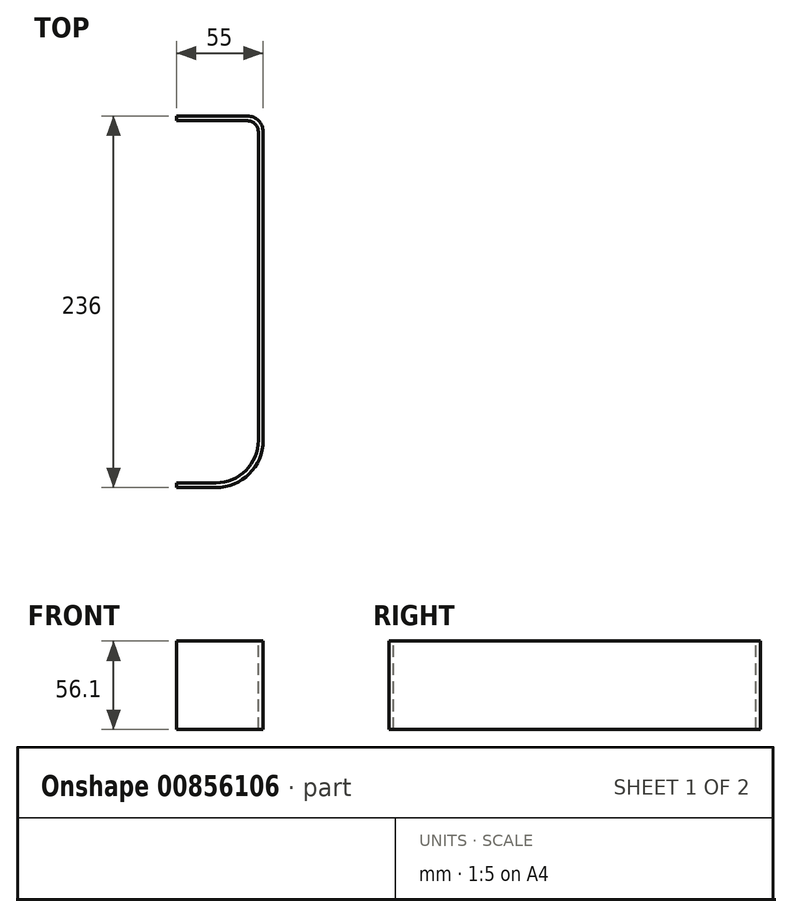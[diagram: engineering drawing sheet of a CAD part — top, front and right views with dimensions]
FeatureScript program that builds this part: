
annotation { "Feature Type Name" : "Feature", "Feature Type Description" : "" }
export const myFeature = defineFeature(function(context is Context, id is Id, definition is map)
    precondition{}
    {
        {
            var Q0;
            Q0=qCreatedBy(makeId("Top.planeOp"),FACE);
            var sketch = newSketch(context, id + "F0", { "sketchPlane" : qUnion([Q0])});
            skLineSegment(sketch, "E0.1", {"start": v(0, 0) * mm, "end": v(0, 0) * mm});
            skPoint(sketch, "E1", {"position": v(265.17, 265.17) * mm});
            skPoint(sketch, "E2", {"position": v(-265.17, 265.17) * mm});
            skPoint(sketch, "E3", {"position": v(265.17, -265.17) * mm});
            skCircle(sketch, "E4", {"center": v(265.17, 265.17) * mm, "radius": 234.95 * mm, "construction": true});
            skCircle(sketch, "E5", {"center": v(265.17, -265.17) * mm, "radius": 234.95 * mm, "construction": true});
            skCircle(sketch, "E6", {"center": v(265.17, 265.17) * mm, "radius": 30.35 * mm, "construction": true});
            skCircle(sketch, "E7", {"center": v(265.17, -265.17) * mm, "radius": 30.35 * mm, "construction": true});
            skLineSegment(sketch, "E8", {"start": v(0, 0) * mm, "end": v(265.17, 265.17) * mm, "construction": true});
            skLineSegment(sketch, "E9", {"start": v(0, 0) * mm, "end": v(265.17, -265.17) * mm, "construction": true});
            skArc(sketch, "E10", {"start": v(-265.17, 265.17) * mm, "mid": v(265.17, 265.17) * mm, "end": v(265.17, -265.17) * mm, "construction": true});
            skPoint(sketch, "E11", {"position": v(235.63, -235.63) * mm});
            skLineSegment(sketch, "E12", {"start": v(242.7, -228.56) * mm, "end": v(217.95, -203.81) * mm});
            skLineSegment(sketch, "E13", {"start": v(217.95, -203.81) * mm, "end": v(203.81, -217.95) * mm});
            skLineSegment(sketch, "E14", {"start": v(242.7, -228.56) * mm, "end": v(228.56, -242.7) * mm});
            skLineSegment(sketch, "E15", {"start": v(228.56, -242.7) * mm, "end": v(203.81, -217.95) * mm});
            skLineSegment(sketch, "E16.left", {"start": v(55, -103) * mm, "end": v(55, 93) * mm});
            skPoint(sketch, "E17.visualSharp", {"position": v(55, -133) * mm});
            skArc(sketch, "E17.filletArc", {"start": v(25, -133) * mm, "mid": v(46.21, -124.21) * mm, "end": v(55, -103) * mm});
            skPoint(sketch, "E18.visualSharp", {"position": v(55, 103) * mm});
            skArc(sketch, "E18.filletArc", {"start": v(55, 93) * mm, "mid": v(52.07, 100.07) * mm, "end": v(45, 103) * mm});
            skPoint(sketch, "E19", {"position": v(0, 103) * mm});
            skPoint(sketch, "E20", {"position": v(0, -133) * mm});
            skLineSegment(sketch, "E21", {"start": v(0, -133) * mm, "end": v(0, -130) * mm});
            skLineSegment(sketch, "E22", {"start": v(0, -130) * mm, "end": v(25, -130) * mm});
            skLineSegment(sketch, "E23", {"start": v(52, 93) * mm, "end": v(52, -103) * mm});
            skLineSegment(sketch, "E24", {"start": v(0, 103) * mm, "end": v(0, 100) * mm});
            skLineSegment(sketch, "E25", {"start": v(0, 100) * mm, "end": v(45, 100) * mm});
            skArc(sketch, "E26", {"start": v(45, 100) * mm, "mid": v(49.95, 97.95) * mm, "end": v(52, 93) * mm});
            skArc(sketch, "E27", {"start": v(52, -103) * mm, "mid": v(44.1, -122.1) * mm, "end": v(25, -130) * mm});
            skLineSegment(sketch, "E28", {"start": v(0, 103) * mm, "end": v(45, 103) * mm});
            skLineSegment(sketch, "E29", {"start": v(0, -133) * mm, "end": v(25, -133) * mm});
            skLineSegment(sketch, "E30", {"start": v(0, 100) * mm, "end": v(0, -130) * mm, "construction": true});
            skLineSegment(sketch, "E31", {"start": v(0, 0) * mm, "end": v(55, 0) * mm, "construction": true});
            skPoint(sketch, "E32", {"position": v(55, 0) * mm});
            skSolve(sketch);
        }
        {
            var Q0;
            Q0=makeQuery(id+"F0.imprint","IMPRINT",FACE,{"disambiguationData":[TD([[makeQuery(id+"F0.imprint","IMPRINT",EDGE,{"derivedFrom":sQuery(id+"F0.wireOp",EDGE,"E16.left")}),1.0]])]});
            extrude(context, id + "F1", {"entities" : qUnion([Q0]), "oppositeDirection" : true, "depth" : 18 * mm, "offsetDistance" : 25 * mm, "hasSecondDirection" : true, "secondDirectionOppositeDirection" : false, "secondDirectionDepth" : 38.1 * mm});
        }
        {
            var Q0;
            Q0=sQuery(id+"F0.wireOp",EDGE,"E9");
            var Q1;
            Q1=qCreatedBy(makeId("Top.planeOp"),FACE);
            cPlane(context, id + "F2", {"entities" : qUnion([Q0, Q1]), "cplaneType" : CPlaneType.LINE_ANGLE, "offset" : 25 * mm, "angle" : 90 * degree, "oppositeDirection" : true, "width" : 150 * mm, "height" : 150 * mm});
        }
    });
